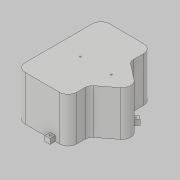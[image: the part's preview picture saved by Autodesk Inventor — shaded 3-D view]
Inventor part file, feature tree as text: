
AUTODESK INVENTOR PART (.ipt)
format: ipt  version: 2019 (Build 230136000, 136)  size: 376,320 bytes
history: native  units: mm
features: extrude x6, sketch x6, draft x1, fillet x1, shell x1, boolean_combine x1, delete_face x1
ambient origin geometry x8: Origin, YZ Plane, XZ Plane, XY Plane, X Axis, Y Axis, Z Axis, Center Point
bodies: Solid1 (feature_tree), Solid2 (feature_tree)
feature tree (17):
  extrude  "Extrusion1"  Depth=200.0mm
  extrude  "Extrusion2"  Depth=42.0mm
  extrude  "Extrusion3"  TaperAngle=75.0deg  [1 undecoded]
  draft  "FaceDraft1"
  fillet  "Fillet1"  Radius=52.0mm
  shell  "Shell2"  Thickness=110.0mm
  extrude  "Extrusion4"  Depth=77.0mm
  boolean_combine  "Combine1"
  delete_face  "Delete Face1"
  extrude  "Extrusion5"  Depth=110.0mm TaperAngle=0.0deg
  extrude  "Extrusion6"  Depth=15.0mm
  sketch  "Sketch1"  dims[d0=100.0mm d1=200.0mm]
  sketch  "Sketch2"  dims[d2=35.0mm d4=42.0mm]
  sketch  "Sketch3"  dims[d5=42.0mm d6=75.0deg d7=52.0mm d8=110.0mm d9=0.0mm]
  sketch  "Sketch5"  dims[d11=62.0mm d12=77.0mm]
  sketch  "Sketch6"  dims[d13=110.0mm d14=0.0mm d22=110.0mm d23=0.0mm]
  sketch  "Sketch7"  dims[d25=0.698132mm d26=5.0mm d27=1.0mm d28=4.0mm d29=20.000002mm d30=20.0mm d31=20.0mm d32=130.0mm d33=0.0mm d34=15.0mm d35=30.0mm d36=30.0mm d37=15.0mm d38=15.0mm d39=30.0mm d40=20.0mm d41=40.0mm d42=5.0mm d43=7.5mm d44=5.0mm d45=7.5mm d46=7.5mm d47=5.0mm d48=7.5mm d49=7.5mm d50=15.0mm d51=0.0mm d52=200.0mm d53=4.0mm d54=4.0mm d55=65.0mm d56=90.0mm d57=0.0mm d58=0.0mm]
note: 1 required parameter value undecoded (feature->parameter linkage not recoverable at this tier; creation-order binding heuristic only, values carry confidence <= 0.55)
